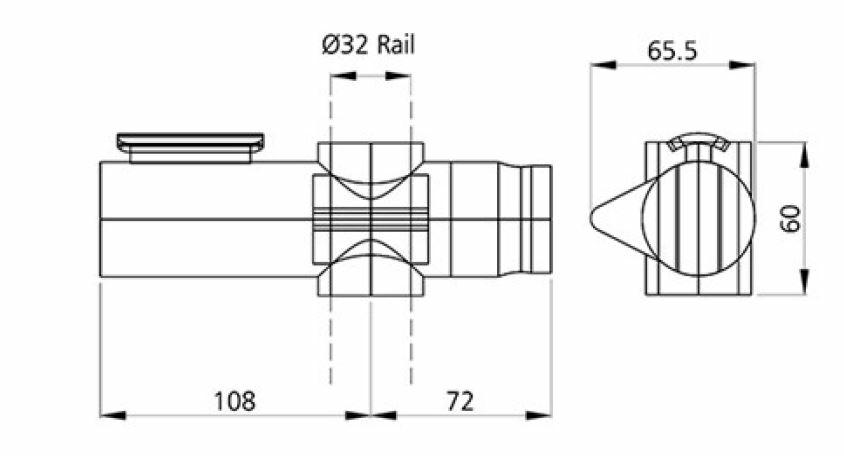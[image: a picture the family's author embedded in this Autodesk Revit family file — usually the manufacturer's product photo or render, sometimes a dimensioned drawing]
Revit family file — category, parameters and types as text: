
# Revit family: RBA4805-731
name_source: partatom
category: Plumbing Fixtures
units: mm (PartAtom-declared; Revit-internal decimal feet)

## family parameters
Always vertical = Yes
Cut with Voids When Loaded = No
Part Type = Normal
Room Calculation Point = No
Round Connector Dimension = Use Diameter
Shared = Yes
Work Plane-Based = No

## types (1)
- RBA4805-731
    CW Connection = Yes
    Default Elevation = 0 mm  [stored 0 ft]
    Description = Modular Shower Rail Kit, Satin
    Distance Away from Toilet (default) = 1090 mm  [stored 3.57612 ft]
    Distance Away from Wall (default) = 100 mm  [stored 0.328084 ft]
    HW Connection = Yes
    Manufacturer = RBA Group
    Materials & Finishes = PVD Brushed Brass Stainless Steel
    Model = RBA4801-731
    OFFSET = 1000 mm  [stored 3.28084 ft]
    URL = www.rba.com.au
    Vent Connection = Yes
    Waste Connection = Yes

note: [stored X ft] marks values corroborated as IEEE doubles in the binary element streams (Revit-internal decimal feet)

## geometry (parser evidence)
native form markers: Blend x2, Sweep x5
no freeform markers — native parametric forms only
